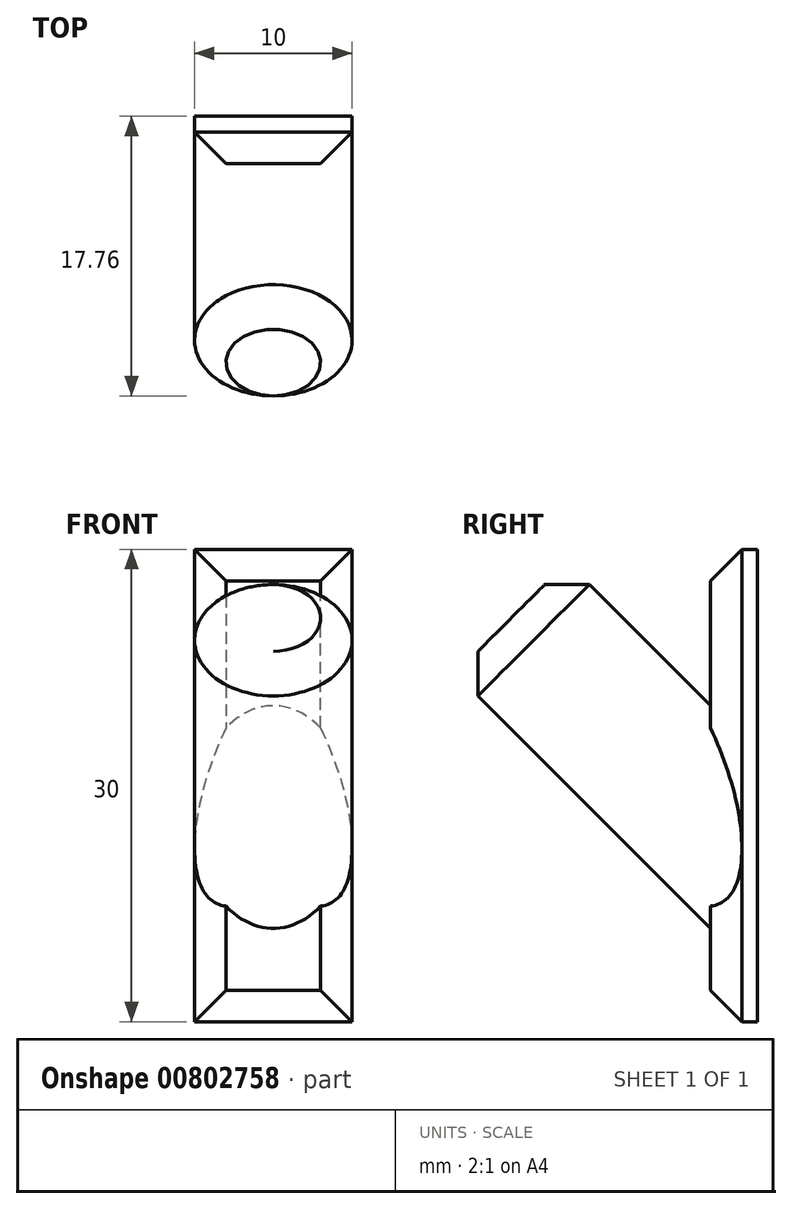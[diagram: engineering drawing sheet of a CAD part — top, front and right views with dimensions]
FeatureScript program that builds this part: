
annotation { "Feature Type Name" : "Feature", "Feature Type Description" : "" }
export const myFeature = defineFeature(function(context is Context, id is Id, definition is map)
    precondition{}
    {
        {
            var Q0;
            Q0=qCreatedBy(makeId("Front.planeOp"),FACE);
            var sketch = newSketch(context, id + "F0", { "sketchPlane" : qUnion([Q0])});
            skLineSegment(sketch, "E0.bottom", {"start": v(-5, 20) * mm, "end": v(5, 20) * mm});
            skLineSegment(sketch, "E0.top", {"start": v(-5, -10) * mm, "end": v(5, -10) * mm});
            skLineSegment(sketch, "E0.left", {"start": v(-5, 20) * mm, "end": v(-5, -10) * mm});
            skLineSegment(sketch, "E0.right", {"start": v(5, 20) * mm, "end": v(5, -10) * mm});
            skSolve(sketch);
        }
        {
            var Q0;
            Q0 = qSketchRegion(id + "F0", true);
            extrude(context, id + "F1", {"entities" : qUnion([Q0]), "depth" : 3 * mm, "offsetDistance" : 25 * mm});
        }
        {
            var Q0;
            Q0=makeQuery(id+"F1.opExtrude","CAP_FACE",FACE,{"disambiguationData":[OSD([sQuery(id+"F0.wireOp",EDGE,"E0.bottom"),sQuery(id+"F0.wireOp",EDGE,"E0.top"),sQuery(id+"F0.wireOp",EDGE,"E0.left"),sQuery(id+"F0.wireOp",EDGE,"E0.right")])],"isStart":false});
            var sketch = newSketch(context, id + "F2", { "sketchPlane" : qUnion([Q0])});
            skLineSegment(sketch, "E1", {"start": v(-6.42, 0) * mm, "end": v(9.7, 0) * mm, "construction": true});
            skSolve(sketch);
        }
        {
            var Q0;
            Q0=qCreatedBy(makeId("Origin.pointOp"),VERTEX);
            var Q1;
            Q1=sQuery(id+"F2.wireOp",EDGE,"E1");
            cPlane(context, id + "F3", {"entities" : qUnion([Q0, Q1]), "cplaneType" : CPlaneType.LINE_ANGLE, "offset" : 25 * mm, "angle" : 45 * degree, "width" : 150 * mm, "height" : 150 * mm});
        }
        {
            var Q0;
            Q0=qCreatedBy(id+"F3.planeOp",FACE);
            var sketch = newSketch(context, id + "F4", { "sketchPlane" : qUnion([Q0])});
            skCircle(sketch, "E2", {"center": v(0, 0) * mm, "radius": 5 * mm});
            skSolve(sketch);
        }
        {
            var Q0;
            Q0 = qSketchRegion(id + "F4", true);
            extrude(context, id + "F5", {"entities" : qUnion([Q0]), "operationType" : NewBodyOperationType.ADD, "depth" : 20 * mm, "offsetDistance" : 25 * mm, "hasSecondDirection" : true, "secondDirectionOppositeDirection" : true, "secondDirectionDepth" : 5 * mm});
        }
        {
            var Q0;
            {var subQ0=sQuery(id+"F0.wireOp",EDGE,"E0.bottom");var subQ1=sQuery(id+"F0.wireOp",EDGE,"E0.left");Q0=makeQuery(id+"F5.boolean.opBoolean","SPLIT",EDGE,{"disambiguationData":[TD([makeQuery(id+"F1.opExtrude","SWEPT_FACE",FACE,{"disambiguationData":[OSD([subQ0])]})])],"derivedFrom":makeQuery(id+"F1.opExtrude","CAP_EDGE",EDGE,{"disambiguationData":[OSD([subQ1])],"isStart":false})});}
            var Q1;
            Q1=makeQuery(id+"F5.opExtrude","CAP_EDGE",EDGE,{"disambiguationData":[OSD([sQuery(id+"F4.wireOp",EDGE,"E2")])],"isStart":false});
            var Q2;
            Q2=makeQuery(id+"F1.opExtrude","CAP_EDGE",EDGE,{"disambiguationData":[OSD([sQuery(id+"F0.wireOp",EDGE,"E0.bottom")])],"isStart":false});
            var Q3;
            Q3=makeQuery(id+"F1.opExtrude","CAP_EDGE",EDGE,{"disambiguationData":[OSD([sQuery(id+"F0.wireOp",EDGE,"E0.top")])],"isStart":false});
            var Q4;
            {var subQ0=sQuery(id+"F0.wireOp",EDGE,"E0.bottom");var subQ1=sQuery(id+"F0.wireOp",EDGE,"E0.right");Q4=makeQuery(id+"F5.boolean.opBoolean","SPLIT",EDGE,{"disambiguationData":[TD([makeQuery(id+"F1.opExtrude","SWEPT_FACE",FACE,{"disambiguationData":[OSD([subQ0])]})])],"derivedFrom":makeQuery(id+"F1.opExtrude","CAP_EDGE",EDGE,{"disambiguationData":[OSD([subQ1])],"isStart":false})});}
            chamfer(context, id + "F6", {"entities" : qUnion([Q0, Q1, Q2, Q3, Q4]), "width" : 2 * mm, "tangentPropagation" : true});
        }
        {
            var Q0;
            Q0=makeQuery(id+"F0.imprint","IMPRINT",FACE,{"disambiguationData":[TD([[makeQuery(id+"F0.imprint","IMPRINT",EDGE,{"derivedFrom":sQuery(id+"F0.wireOp",EDGE,"E0.bottom")}),-1.0]])]});
            extrude(context, id + "F7", {"entities" : qUnion([Q0]), "operationType" : NewBodyOperationType.REMOVE, "oppositeDirection" : true, "depth" : 25 * mm, "offsetDistance" : 25 * mm});
        }
    });
